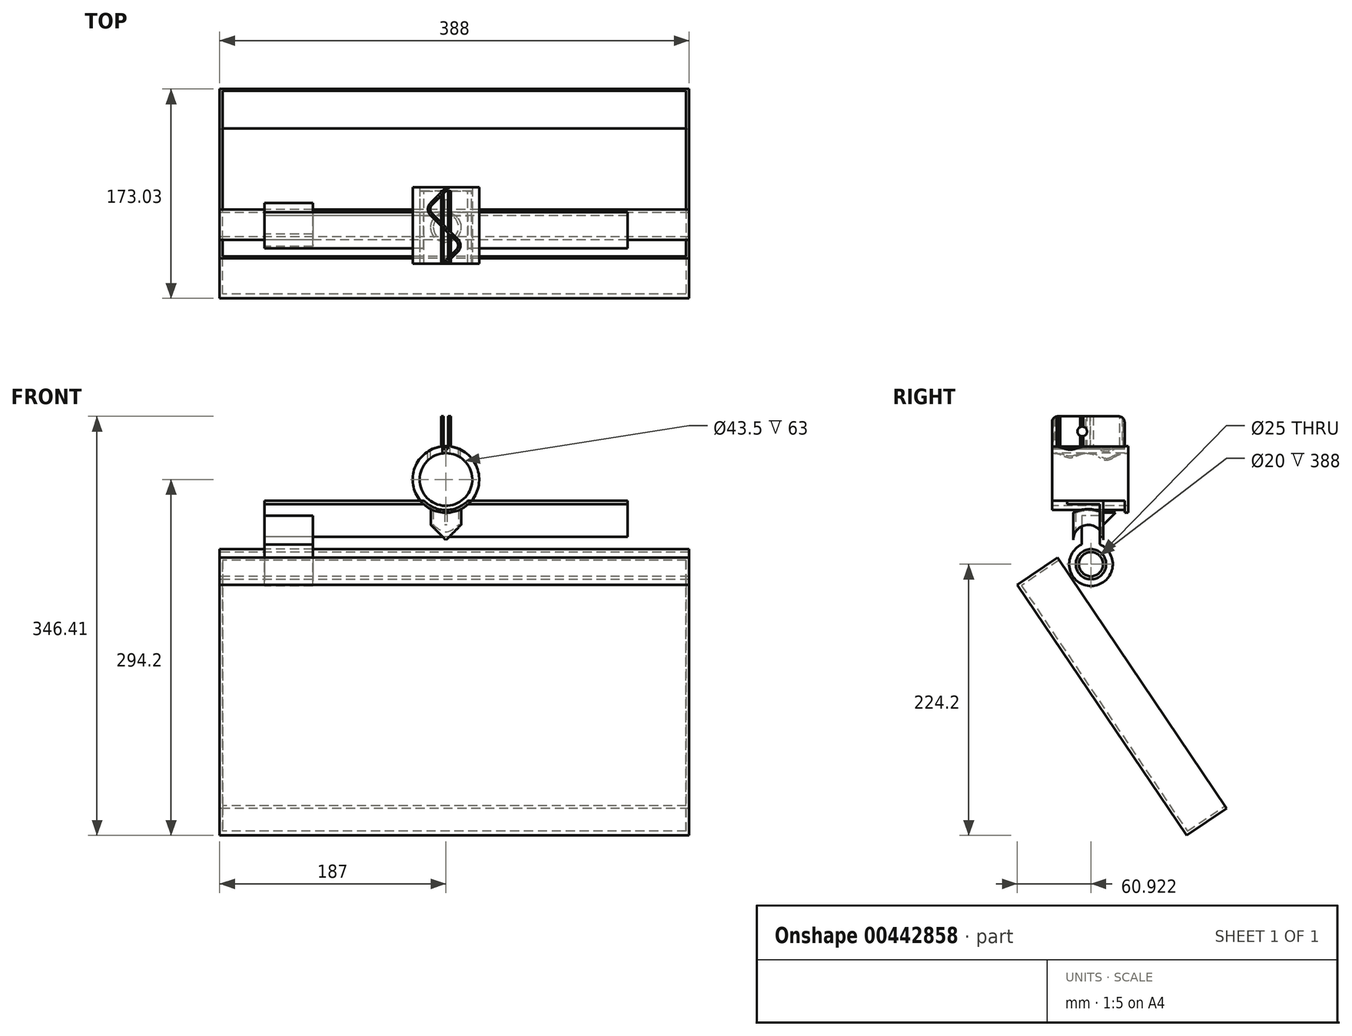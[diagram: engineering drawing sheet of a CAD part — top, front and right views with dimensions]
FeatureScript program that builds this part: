
annotation { "Feature Type Name" : "Feature", "Feature Type Description" : "" }
export const myFeature = defineFeature(function(context is Context, id is Id, definition is map)
    precondition{}
    {
        {
            var Q0;
            Q0=qCreatedBy(makeId("Right.planeOp"),FACE);
            var sketch = newSketch(context, id + "F0", { "sketchPlane" : qUnion([Q0])});
            skCircle(sketch, "E0", {"center": v(0, 0) * mm, "radius": 12.5 * mm});
            skCircle(sketch, "E1", {"center": v(0, 0) * mm, "radius": 10.5 * mm});
            skSolve(sketch);
        }
        {
            var Q0;
            Q0=makeQuery(id+"F0.imprint","IMPRINT",FACE,{"disambiguationData":[TD([[makeQuery(id+"F0.imprint","IMPRINT",EDGE,{"derivedFrom":sQuery(id+"F0.wireOp",EDGE,"E0")}),1.0]])]});
            extrude(context, id + "F1", {"entities" : qUnion([Q0]), "depth" : 400 * mm, "symmetric" : true});
        }
        {
            var Q0;
            Q0=qCreatedBy(makeId("Front.planeOp"),FACE);
            var sketch = newSketch(context, id + "F2", { "sketchPlane" : qUnion([Q0])});
            skCircle(sketch, "E2", {"center": v(0, 50) * mm, "radius": 27.5 * mm});
            skCircle(sketch, "E3", {"center": v(0, 50) * mm, "radius": 25.25 * mm});
            skSolve(sketch);
        }
        {
            var Q0;
            Q0=makeQuery(id+"F2.imprint","IMPRINT",FACE,{"disambiguationData":[TD([[makeQuery(id+"F2.imprint","IMPRINT",EDGE,{"derivedFrom":sQuery(id+"F2.wireOp",EDGE,"E2")}),1.0]])]});
            extrude(context, id + "F3", {"entities" : qUnion([Q0]), "depth" : 30 * mm, "hasSecondDirection" : true, "secondDirectionOppositeDirection" : true, "secondDirectionDepth" : 30 * mm, "offsetDistance" : 25 * mm});
        }
        {
            var Q0;
            Q0=qCreatedBy(makeId("Top.planeOp"),FACE);
            var sketch = newSketch(context, id + "F4", { "sketchPlane" : qUnion([Q0])});
            skCircle(sketch, "E4", {"center": v(0, 0) * mm, "radius": 12.5 * mm});
            skCircle(sketch, "E5", {"center": v(0, 0) * mm, "radius": 10.5 * mm});
            skSolve(sketch);
        }
        {
            var Q0;
            Q0=makeQuery(id+"F4.imprint","IMPRINT",FACE,{"disambiguationData":[TD([[makeQuery(id+"F4.imprint","IMPRINT",EDGE,{"derivedFrom":sQuery(id+"F4.wireOp",EDGE,"E4")}),1.0]])]});
            var Q1;
            Q1=makeQuery(id+"F3.opExtrude","SWEPT_FACE",FACE,{"disambiguationData":[OSD([sQuery(id+"F2.wireOp",EDGE,"E2")])]});
            extrude(context, id + "F5", {"entities" : qUnion([Q0]), "endBound" : BoundingType.UP_TO_SURFACE, "endBoundEntityFace" : qUnion([Q1]), "depth" : 25 * mm});
        }
        {
            var Q0;
            Q0=makeQuery(id+"F0.imprint","IMPRINT",FACE,{"disambiguationData":[TD([[makeQuery(id+"F0.imprint","IMPRINT",EDGE,{"derivedFrom":sQuery(id+"F0.wireOp",EDGE,"E1")}),1.0]])]});
            var Q1;
            Q1=makeQuery(id+"F0.imprint","IMPRINT",FACE,{"disambiguationData":[TD([[makeQuery(id+"F0.imprint","IMPRINT",EDGE,{"derivedFrom":sQuery(id+"F0.wireOp",EDGE,"E0")}),1.0]])]});
            extrude(context, id + "F6", {"entities" : qUnion([Q0, Q1]), "operationType" : NewBodyOperationType.REMOVE, "endBound" : BoundingType.THROUGH_ALL, "oppositeDirection" : true, "depth" : 25 * mm, "hasSecondDirection" : true, "secondDirectionBound" : BoundingType.THROUGH_ALL, "secondDirectionOppositeDirection" : false, "secondDirectionDepth" : 25 * mm});
        }
        {
            var Q0;
            Q0=qCreatedBy(makeId("Front.planeOp"),FACE);
            var sketch = newSketch(context, id + "F7", { "sketchPlane" : qUnion([Q0])});
            skLineSegment(sketch, "E6", {"start": v(0, 0) * mm, "end": v(0, 149.4) * mm, "construction": true});
            skLineSegment(sketch, "E7.bottom", {"start": v(2, 60) * mm, "end": v(-2, 60) * mm});
            skLineSegment(sketch, "E7.top", {"start": v(2, 125) * mm, "end": v(-2, 125) * mm});
            skLineSegment(sketch, "E7.left", {"start": v(2, 60) * mm, "end": v(2, 125) * mm});
            skLineSegment(sketch, "E7.right", {"start": v(-2, 60) * mm, "end": v(-2, 125) * mm});
            skPoint(sketch, "E7.middle", {"position": v(0, 92.5) * mm});
            skSolve(sketch);
        }
        {
            var Q0;
            Q0 = qSketchRegion(id + "F7", true);
            extrude(context, id + "F8", {"entities" : qUnion([Q0]), "operationType" : NewBodyOperationType.REMOVE, "endBound" : BoundingType.THROUGH_ALL, "oppositeDirection" : true, "depth" : 25 * mm, "hasSecondDirection" : true, "secondDirectionBound" : BoundingType.THROUGH_ALL, "secondDirectionOppositeDirection" : false, "secondDirectionDepth" : 25 * mm, "offsetDistance" : 25 * mm});
        }
        {
            var Q0;
            Q0=qCreatedBy(makeId("Front.planeOp"),FACE);
            var sketch = newSketch(context, id + "F9", { "sketchPlane" : qUnion([Q0])});
            skArc(sketch, "E8.0", {"start": v(-2, 77.43) * mm, "mid": v(-3, 77.34) * mm, "end": v(-4, 77.2) * mm});
            skLineSegment(sketch, "E9", {"start": v(-2, 77.43) * mm, "end": v(-2, 102.2) * mm});
            skLineSegment(sketch, "E10", {"start": v(-2, 102.2) * mm, "end": v(-4, 102.2) * mm});
            skLineSegment(sketch, "E11", {"start": v(-4, 102.2) * mm, "end": v(-4, 77.2) * mm});
            skLineSegment(sketch, "E12", {"start": v(2, 77.43) * mm, "end": v(2, 102.2) * mm});
            skLineSegment(sketch, "E13", {"start": v(2, 102.2) * mm, "end": v(4, 102.2) * mm});
            skLineSegment(sketch, "E14", {"start": v(4, 102.2) * mm, "end": v(4, 77.2) * mm});
            skArc(sketch, "E15.trimOffspring", {"start": v(4, 77.2) * mm, "mid": v(3, 77.34) * mm, "end": v(2, 77.43) * mm});
            skSolve(sketch);
        }
        {
            var Q0;
            Q0 = qSketchRegion(id + "F9", true);
            var Q1;
            Q1=makeQuery(id+"F3.opExtrude","CAP_FACE",FACE,{"disambiguationData":[OSD([sQuery(id+"F2.wireOp",EDGE,"E2"),sQuery(id+"F2.wireOp",EDGE,"E3")])],"isStart":false});
            var Q2;
            Q2=makeQuery(id+"F3.opExtrude","CAP_FACE",FACE,{"disambiguationData":[OSD([sQuery(id+"F2.wireOp",EDGE,"E2"),sQuery(id+"F2.wireOp",EDGE,"E3")])],"isStart":true});
            extrude(context, id + "F10", {"entities" : qUnion([Q0]), "endBound" : BoundingType.UP_TO_SURFACE, "endBoundEntityFace" : qUnion([Q1]), "depth" : 50 * mm, "hasSecondDirection" : true, "secondDirectionBound" : BoundingType.UP_TO_SURFACE, "secondDirectionOppositeDirection" : true, "secondDirectionBoundEntityFace" : qUnion([Q2]), "secondDirectionDepth" : 10 * mm, "offsetDistance" : 25 * mm});
        }
        {
            var Q0;
            Q0=makeQuery(id+"F10.opExtrude","SWEPT_FACE",FACE,{"disambiguationData":[OSD([sQuery(id+"F9.wireOp",EDGE,"E11")])]});
            var sketch = newSketch(context, id + "F11", { "sketchPlane" : qUnion([Q0])});
            skCircle(sketch, "E16", {"center": v(5, 89.7) * mm, "radius": 4 * mm});
            skPoint(sketch, "E16.centerSnap0", {"position": v(7.5, 74.68) * mm});
            skSolve(sketch);
        }
        {
            var Q0;
            Q0=sQuery(id+"F11.wireOp",VERTEX,"E16.center");
            var Q1;
            Q1=makeQuery(id+"F10.opExtrude","SWEPT_BODY",BODY,{"disambiguationData":[OSD([sQuery(id+"F9.wireOp",EDGE,"E12"),sQuery(id+"F9.wireOp",EDGE,"E13"),sQuery(id+"F9.wireOp",EDGE,"E14"),sQuery(id+"F9.wireOp",EDGE,"E15.trimOffspring")])]});
            var Q2;
            Q2=makeQuery(id+"F10.opExtrude","SWEPT_BODY",BODY,{"disambiguationData":[OSD([sQuery(id+"F9.wireOp",EDGE,"E8.0"),sQuery(id+"F9.wireOp",EDGE,"E9"),sQuery(id+"F9.wireOp",EDGE,"E10"),sQuery(id+"F9.wireOp",EDGE,"E11")])]});
            hole(context, id + "F12", {"style" : HoleStyle.SIMPLE, "endStyle" : HoleEndStyle.THROUGH, "holeDiameter" : 8 * mm, "isTappedThrough" : true, "tappedDepth" : 12 * mm, "tapClearance" : 3, "locations" : qUnion([Q0]), "scope" : qUnion([Q1, Q2])});
        }
        {
            var Q0;
            Q0=makeQuery(id+"F10.opExtrude","CAP_EDGE",EDGE,{"disambiguationData":[OSD([sQuery(id+"F9.wireOp",EDGE,"E10")])],"isStart":false});
            var Q1;
            Q1=makeQuery(id+"F10.opExtrude","CAP_EDGE",EDGE,{"disambiguationData":[OSD([sQuery(id+"F9.wireOp",EDGE,"E13")])],"isStart":false});
            var Q2;
            Q2=makeQuery(id+"F10.opExtrude","CAP_EDGE",EDGE,{"disambiguationData":[OSD([sQuery(id+"F9.wireOp",EDGE,"E13")])],"isStart":true});
            var Q3;
            Q3=makeQuery(id+"F10.opExtrude","CAP_EDGE",EDGE,{"disambiguationData":[OSD([sQuery(id+"F9.wireOp",EDGE,"E10")])],"isStart":true});
            var Q4;
            Q4=makeQuery(id+"F10.opExtrude","CAP_EDGE",EDGE,{"disambiguationData":[OSD([sQuery(id+"F9.wireOp",EDGE,"E13")])],"isStart":true});
            var Q5;
            Q5=makeQuery(id+"F10.opExtrude","CAP_EDGE",EDGE,{"disambiguationData":[OSD([sQuery(id+"F9.wireOp",EDGE,"E10")])],"isStart":true});
            fillet(context, id + "F13", {"entities" : qUnion([Q0, Q1, Q2, Q3, Q4, Q5]), "radius" : 5 * mm, "tangentPropagation" : true, "allowEdgeOverflow" : false});
        }
        {
            var Q0;
            Q0=qCreatedBy(makeId("Right.planeOp"),FACE);
            var sketch = newSketch(context, id + "F14", { "sketchPlane" : qUnion([Q0])});
            skLineSegment(sketch, "E17", {"start": v(22.5, 22.5) * mm, "end": v(12.5, 22.5) * mm});
            skLineSegment(sketch, "E18", {"start": v(12.5, 22.5) * mm, "end": v(12.5, 12.5) * mm});
            skLineSegment(sketch, "E19", {"start": v(12.5, 12.5) * mm, "end": v(22.5, 22.5) * mm});
            skSolve(sketch);
        }
        {
            var Q0;
            Q0 = qSketchRegion(id + "F14", true);
            extrude(context, id + "F15", {"entities" : qUnion([Q0]), "operationType" : NewBodyOperationType.ADD, "depth" : 2 * mm, "symmetric" : true});
        }
        {
            var Q0;
            Q0=qCreatedBy(makeId("Right.planeOp"),FACE);
            var sketch = newSketch(context, id + "F16", { "sketchPlane" : qUnion([Q0])});
            skLineSegment(sketch, "E20", {"start": v(-17.5, 32.5) * mm, "end": v(12.5, 32.5) * mm});
            skLineSegment(sketch, "E21", {"start": v(12.5, 32.5) * mm, "end": v(12.5, 2.5) * mm});
            skLineSegment(sketch, "E22", {"start": v(12.5, 2.5) * mm, "end": v(9.5, 2.5) * mm});
            skLineSegment(sketch, "E23", {"start": v(9.5, 2.5) * mm, "end": v(9.5, 29.5) * mm});
            skLineSegment(sketch, "E24", {"start": v(9.5, 29.5) * mm, "end": v(-17.5, 29.5) * mm});
            skLineSegment(sketch, "E25", {"start": v(-17.5, 29.5) * mm, "end": v(-17.5, 32.5) * mm});
            skSolve(sketch);
        }
        {
            var Q0;
            Q0 = qSketchRegion(id + "F16", true);
            extrude(context, id + "F17", {"entities" : qUnion([Q0]), "depth" : 300 * mm, "offsetDistance" : 25 * mm, "symmetric" : true});
        }
        {
            var Q0;
            Q0=makeQuery(id+"F17.opExtrude","SWEPT_FACE",FACE,{"disambiguationData":[OSD([sQuery(id+"F16.wireOp",EDGE,"E21")])]});
            var sketch = newSketch(context, id + "F18", { "sketchPlane" : qUnion([Q0])});
            skArc(sketch, "E26.0", {"start": v(21.21, 32.5) * mm, "mid": v(0, 22.5) * mm, "end": v(-21.21, 32.5) * mm});
            skLineSegment(sketch, "E27.0", {"start": v(-21.21, 32.5) * mm, "end": v(21.21, 32.5) * mm});
            skPoint(sketch, "E28.orphan", {"position": v(150, 32.5) * mm});
            skPoint(sketch, "E29.orphan", {"position": v(2, 77.43) * mm});
            skPoint(sketch, "E30.orphan", {"position": v(-150, 32.5) * mm});
            skPoint(sketch, "E31.orphan", {"position": v(-2, 77.43) * mm});
            skSolve(sketch);
        }
        {
            var Q0;
            Q0 = qSketchRegion(id + "F18", true);
            extrude(context, id + "F19", {"entities" : qUnion([Q0]), "operationType" : NewBodyOperationType.REMOVE, "endBound" : BoundingType.THROUGH_ALL, "oppositeDirection" : true, "depth" : 25 * mm, "offsetDistance" : 25 * mm, "hasSecondDirection" : true, "secondDirectionBound" : BoundingType.THROUGH_ALL, "secondDirectionOppositeDirection" : false, "secondDirectionDepth" : 25 * mm});
        }
        {
            var Q0;
            Q0=makeQuery(id+"F17.opExtrude","CAP_FACE",FACE,{"disambiguationData":[OSD([sQuery(id+"F16.wireOp",EDGE,"E20"),sQuery(id+"F16.wireOp",EDGE,"E21"),sQuery(id+"F16.wireOp",EDGE,"E22"),sQuery(id+"F16.wireOp",EDGE,"E23"),sQuery(id+"F16.wireOp",EDGE,"E24"),sQuery(id+"F16.wireOp",EDGE,"E25")])],"isStart":true});
            var sketch = newSketch(context, id + "F20", { "sketchPlane" : qUnion([Q0])});
            skCircle(sketch, "E32", {"center": v(-2.2, -20) * mm, "radius": 12.5 * mm});
            skArc(sketch, "E33", {"start": v(-9.5, -3.55) * mm, "mid": v(-2.43, -38) * mm, "end": v(5.5, -3.73) * mm});
            skLineSegment(sketch, "E34.bottom", {"start": v(-9.5, 20) * mm, "end": v(5.5, 20) * mm});
            skLineSegment(sketch, "E34.left", {"start": v(-9.5, 20) * mm, "end": v(-9.5, -3.55) * mm});
            skLineSegment(sketch, "E34.right", {"start": v(5.5, 20) * mm, "end": v(5.5, -3.73) * mm});
            skSolve(sketch);
        }
        {
            var Q0;
            Q0=makeQuery(id+"F20.imprint","IMPRINT",FACE,{"disambiguationData":[TD([[makeQuery(id+"F20.imprint","IMPRINT",EDGE,{"derivedFrom":sQuery(id+"F20.wireOp",EDGE,"E32")}),-1.0]])]});
            extrude(context, id + "F21", {"entities" : qUnion([Q0]), "oppositeDirection" : true, "depth" : 40 * mm, "offsetDistance" : 25 * mm});
        }
        {
            var Q0;
            Q0=makeQuery(id+"F20.imprint","IMPRINT",FACE,{"disambiguationData":[TD([[makeQuery(id+"F20.imprint","IMPRINT",EDGE,{"derivedFrom":sQuery(id+"F20.wireOp",EDGE,"E32")}),1.0]])]});
            extrude(context, id + "F22", {"entities" : qUnion([Q0]), "oppositeDirection" : true, "depth" : 351 * mm, "offsetDistance" : 25 * mm, "hasSecondDirection" : true, "secondDirectionOppositeDirection" : false, "secondDirectionDepth" : 37 * mm});
        }
        {
            var Q0;
            Q0=makeQuery(id+"F22.opExtrude","CAP_FACE",FACE,{"disambiguationData":[OSD([sQuery(id+"F20.wireOp",EDGE,"E32")])],"isStart":true});
            var sketch = newSketch(context, id + "F23", { "sketchPlane" : qUnion([Q0])});
            skLineSegment(sketch, "E35", {"start": v(25.56, -14.61) * mm, "end": v(-114.31, -221.82) * mm});
            skLineSegment(sketch, "E36", {"start": v(-114.31, -221.82) * mm, "end": v(-81.16, -244.2) * mm});
            skLineSegment(sketch, "E37", {"start": v(-81.16, -244.2) * mm, "end": v(58.72, -37) * mm});
            skLineSegment(sketch, "E38", {"start": v(58.72, -37) * mm, "end": v(25.56, -14.61) * mm});
            skCircle(sketch, "E39", {"center": v(-2.2, -20) * mm, "radius": 12.5 * mm});
            skSolve(sketch);
        }
        {
            var Q0;
            Q0=makeQuery(id+"F23.imprint","IMPRINT",FACE,{"disambiguationData":[TD([[makeQuery(id+"F23.imprint","IMPRINT",EDGE,{"derivedFrom":sQuery(id+"F23.wireOp",EDGE,"E35")}),1.0]])]});
            var Q1;
            Q1=makeQuery(id+"F23.imprint","IMPRINT",FACE,{"disambiguationData":[TD([[makeQuery(id+"F23.imprint","IMPRINT",EDGE,{"derivedFrom":sQuery(id+"F23.wireOp",EDGE,"E39")}),1.0]])]});
            var Q2;
            Q2=makeQuery(id+"F22.opExtrude","CAP_FACE",FACE,{"disambiguationData":[OSD([sQuery(id+"F20.wireOp",EDGE,"E32")])],"isStart":false});
            extrude(context, id + "F24", {"entities" : qUnion([Q0, Q1]), "endBound" : BoundingType.UP_TO_SURFACE, "oppositeDirection" : true, "depth" : 389 * mm, "endBoundEntityFace" : qUnion([Q2]), "offsetDistance" : 25 * mm});
        }
        {
            var Q0;
            Q0=makeQuery(id+"F24.opExtrude","SWEPT_FACE",FACE,{"disambiguationData":[OSD([sQuery(id+"F23.wireOp",EDGE,"E35")])]});
            shell(context, id + "F25", {"entities" : qUnion([Q0]), "thickness" : 2.5 * mm});
        }
        {
            var Q0;
            Q0=makeQuery(id+"F3.opExtrude","CAP_FACE",FACE,{"disambiguationData":[OSD([sQuery(id+"F2.wireOp",EDGE,"E2"),sQuery(id+"F2.wireOp",EDGE,"E3")])],"isStart":false});
            var sketch = newSketch(context, id + "F26", { "sketchPlane" : qUnion([Q0])});
            skArc(sketch, "E40.0", {"start": v(-2, 75.17) * mm, "mid": v(0, 24.75) * mm, "end": v(2, 75.17) * mm, "construction": true});
            skCircle(sketch, "E41", {"center": v(0, 50) * mm, "radius": 25.25 * mm});
            skCircle(sketch, "E42", {"center": v(0, 50) * mm, "radius": 21.75 * mm});
            skSolve(sketch);
        }
        {
            var Q0;
            Q0 = qSketchRegion(id + "F26", true);
            extrude(context, id + "F27", {"entities" : qUnion([Q0]), "oppositeDirection" : true, "depth" : 63 * mm, "offsetDistance" : 25 * mm});
        }
        {
            var Q0;
            Q0=makeQuery(id+"F27.opExtrude","CAP_FACE",FACE,{"disambiguationData":[OSD([sQuery(id+"F26.wireOp",EDGE,"E41"),sQuery(id+"F26.wireOp",EDGE,"E42")])],"isStart":false});
            var sketch = newSketch(context, id + "F28", { "sketchPlane" : qUnion([Q0])});
            skCircle(sketch, "E43.0", {"center": v(0, 50) * mm, "radius": 25.25 * mm});
            skCircle(sketch, "E44", {"center": v(0, 50) * mm, "radius": 27.5 * mm});
            skSolve(sketch);
        }
        {
            var Q0;
            Q0 = qSketchRegion(id + "F28", true);
            extrude(context, id + "F29", {"entities" : qUnion([Q0]), "operationType" : NewBodyOperationType.ADD, "oppositeDirection" : true, "depth" : 3 * mm, "offsetDistance" : 25 * mm});
        }
        {
            var Q0;
            Q0=qCreatedBy(makeId("Top.planeOp"),FACE);
            var Q1;
            Q1=sQuery(id+"F26.wireOp",VERTEX,"E41.center");
            cPlane(context, id + "F30", {"entities" : qUnion([Q0, Q1]), "cplaneType" : CPlaneType.PLANE_POINT, "offset" : 25 * mm, "width" : 150 * mm, "height" : 150 * mm});
        }
        {
            var Q0;
            Q0=qCreatedBy(id+"F30.planeOp",FACE);
            var sketch = newSketch(context, id + "F31", { "sketchPlane" : qUnion([Q0])});
            skLineSegment(sketch, "E45.0", {"start": v(21.75, -30) * mm, "end": v(-21.75, -30) * mm, "construction": true});
            skLineSegment(sketch, "E46.0", {"start": v(20, 33) * mm, "end": v(-20, 33) * mm, "construction": true});
            skLineSegment(sketch, "E47", {"start": v(0, -30) * mm, "end": v(15, -15) * mm});
            skLineSegment(sketch, "E48", {"start": v(15, -15) * mm, "end": v(-15, 15) * mm});
            skLineSegment(sketch, "E49", {"start": v(-15, 15) * mm, "end": v(3, 33) * mm});
            skLineSegment(sketch, "E50", {"start": v(0, -30) * mm, "end": v(-2.83, -30) * mm});
            skLineSegment(sketch, "E51", {"start": v(-2.83, -30) * mm, "end": v(12.17, -15) * mm});
            skLineSegment(sketch, "E52", {"start": v(12.17, -15) * mm, "end": v(-17.83, 15) * mm});
            skLineSegment(sketch, "E53", {"start": v(-17.83, 15) * mm, "end": v(0.17, 33) * mm});
            skLineSegment(sketch, "E54", {"start": v(0.17, 33) * mm, "end": v(3, 33) * mm});
            skSolve(sketch);
        }
        {
            var Q0;
            Q0 = qSketchRegion(id + "F31", true);
            extrude(context, id + "F32", {"entities" : qUnion([Q0]), "operationType" : NewBodyOperationType.REMOVE, "endBound" : BoundingType.THROUGH_ALL, "depth" : 25 * mm, "offsetDistance" : 25 * mm});
        }
        {
            var Q0;
            Q0=makeQuery(id+"F32.boolean.opBoolean","COPY",EDGE,{"derivedFrom":makeQuery(id+"F32.opExtrude","SWEPT_EDGE",EDGE,{"disambiguationData":[OSD([sQuery(id+"F31.wireOp",EDGE,"E51"),sQuery(id+"F31.wireOp",EDGE,"E52")])]})});
            var Q1;
            Q1=makeQuery(id+"F32.boolean.opBoolean","COPY",EDGE,{"derivedFrom":makeQuery(id+"F32.opExtrude","SWEPT_EDGE",EDGE,{"disambiguationData":[OSD([sQuery(id+"F31.wireOp",EDGE,"E48"),sQuery(id+"F31.wireOp",EDGE,"E49")])]})});
            fillet(context, id + "F33", {"entities" : qUnion([Q0, Q1]), "radius" : 5 * mm, "tangentPropagation" : true, "allowEdgeOverflow" : false});
        }
        {
            var Q0;
            Q0=makeQuery(id+"F32.boolean.opBoolean","COPY",EDGE,{"derivedFrom":makeQuery(id+"F32.opExtrude","SWEPT_EDGE",EDGE,{"disambiguationData":[OSD([sQuery(id+"F31.wireOp",EDGE,"E52"),sQuery(id+"F31.wireOp",EDGE,"E53")])]})});
            var Q1;
            Q1=makeQuery(id+"F32.boolean.opBoolean","COPY",EDGE,{"derivedFrom":makeQuery(id+"F32.opExtrude","SWEPT_EDGE",EDGE,{"disambiguationData":[OSD([sQuery(id+"F31.wireOp",EDGE,"E47"),sQuery(id+"F31.wireOp",EDGE,"E48")])]})});
            fillet(context, id + "F34", {"entities" : qUnion([Q0, Q1]), "radius" : 7 * mm, "tangentPropagation" : true, "allowEdgeOverflow" : false});
        }
        {
            var Q0;
            Q0=makeQuery(id+"F24.opExtrude","CAP_FACE",FACE,{"disambiguationData":[OSD([sQuery(id+"F23.wireOp",EDGE,"E39")])],"isStart":false});
            var Q1;
            Q1=makeQuery(id+"F24.opExtrude","CAP_FACE",FACE,{"disambiguationData":[OSD([sQuery(id+"F23.wireOp",EDGE,"E39")])],"isStart":true});
            shell(context, id + "F35", {"entities" : qUnion([Q0, Q1]), "thickness" : 2.5 * mm});
        }
    });
